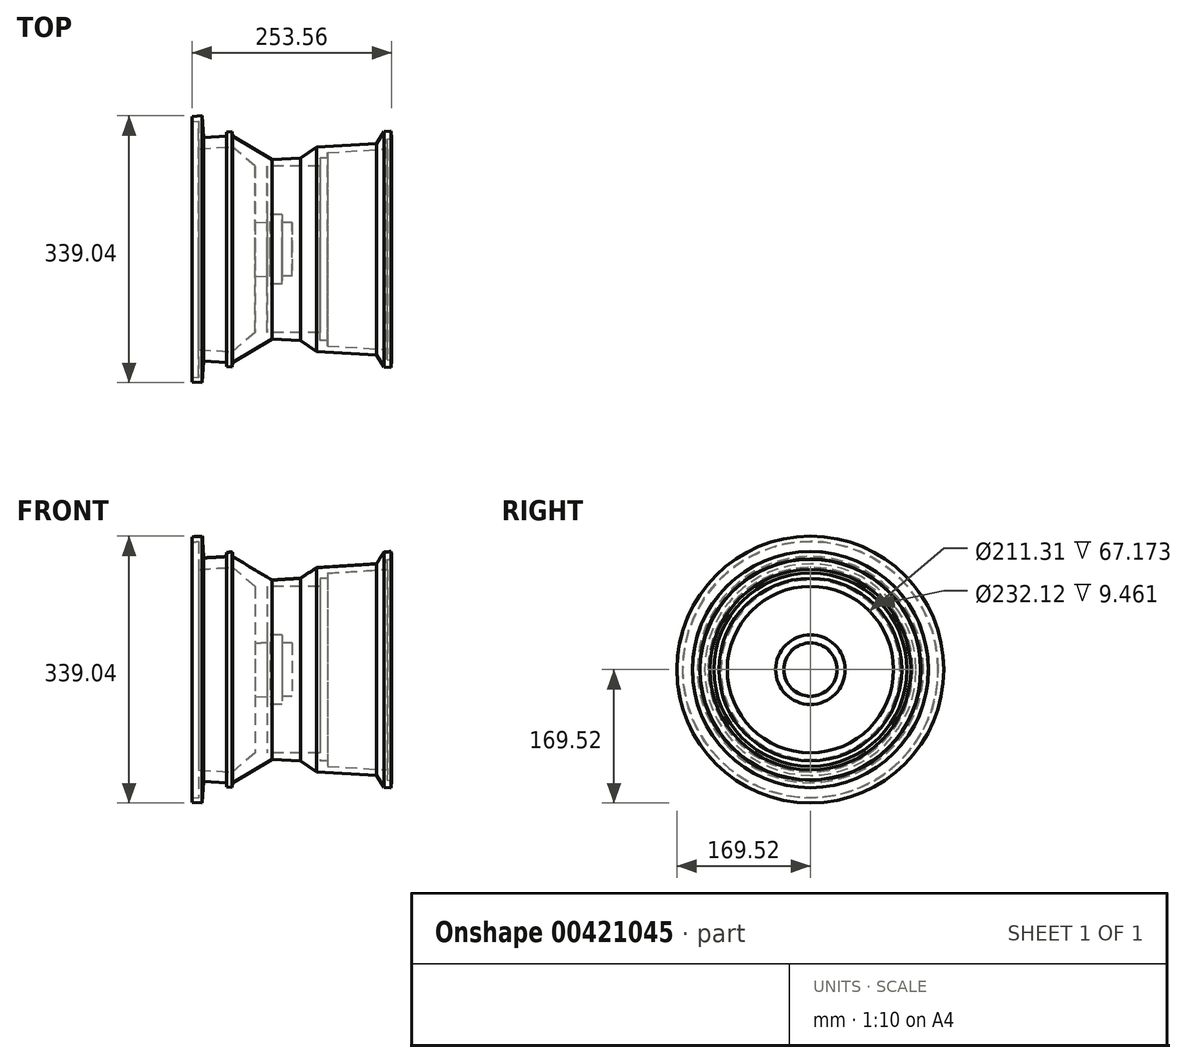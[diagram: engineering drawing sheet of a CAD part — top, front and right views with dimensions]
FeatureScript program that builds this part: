
annotation { "Feature Type Name" : "Feature", "Feature Type Description" : "" }
export const myFeature = defineFeature(function(context is Context, id is Id, definition is map)
    precondition{}
    {
        {
            var Q0;
            Q0=qCreatedBy(makeId("Front.planeOp"),FACE);
            var sketch = newSketch(context, id + "F0", { "sketchPlane" : qUnion([Q0])});
            skLineSegment(sketch, "E0", {"start": v(0, 0) * mm, "end": v(0, 33.75) * mm});
            skLineSegment(sketch, "E1", {"start": v(0, 33.75) * mm, "end": v(-12.72, 33.75) * mm});
            skLineSegment(sketch, "E2", {"start": v(-12.72, 33.75) * mm, "end": v(-12.72, 44.16) * mm});
            skLineSegment(sketch, "E3", {"start": v(-12.72, 44.16) * mm, "end": v(-31.64, 44.16) * mm});
            skLineSegment(sketch, "E4", {"start": v(-31.64, 44.16) * mm, "end": v(-31.64, 105.65) * mm});
            skLineSegment(sketch, "E5", {"start": v(-31.64, 105.65) * mm, "end": v(35.53, 105.65) * mm});
            skLineSegment(sketch, "E6", {"start": v(35.53, 105.65) * mm, "end": v(35.53, 116.06) * mm});
            skLineSegment(sketch, "E7", {"start": v(35.53, 116.06) * mm, "end": v(45, 116.06) * mm});
            skLineSegment(sketch, "E8", {"start": v(45, 116.06) * mm, "end": v(45, 122.68) * mm});
            skLineSegment(sketch, "E9", {"start": v(45, 122.68) * mm, "end": v(121.63, 127.41) * mm});
            skLineSegment(sketch, "E10", {"start": v(121.63, 127.41) * mm, "end": v(120.84, 140.06) * mm});
            skLineSegment(sketch, "E11", {"start": v(120.84, 140.06) * mm, "end": v(126.7, 140.42) * mm});
            skLineSegment(sketch, "E12", {"start": v(126.7, 140.42) * mm, "end": v(126.1, 150) * mm});
            skLineSegment(sketch, "E13", {"start": v(126.1, 150) * mm, "end": v(117.12, 149.44) * mm});
            skLineSegment(sketch, "E14", {"start": v(117.12, 149.44) * mm, "end": v(107.32, 134.35) * mm});
            skLineSegment(sketch, "E15", {"start": v(107.32, 134.35) * mm, "end": v(31.6, 129.67) * mm});
            skLineSegment(sketch, "E16", {"start": v(31.6, 129.67) * mm, "end": v(10.77, 116.06) * mm});
            skLineSegment(sketch, "E17", {"start": v(10.77, 116.06) * mm, "end": v(-25.33, 113.83) * mm});
            skLineSegment(sketch, "E18", {"start": v(-25.33, 113.83) * mm, "end": v(-75.4, 143.7) * mm});
            skLineSegment(sketch, "E19", {"start": v(-75.4, 143.7) * mm, "end": v(-75.76, 149.44) * mm});
            skLineSegment(sketch, "E20", {"start": v(-75.76, 149.44) * mm, "end": v(-83.2, 148.98) * mm});
            skLineSegment(sketch, "E21", {"start": v(-83.2, 148.98) * mm, "end": v(-82.87, 143.7) * mm});
            skLineSegment(sketch, "E22", {"start": v(-82.87, 143.7) * mm, "end": v(-112.12, 141.89) * mm});
            skLineSegment(sketch, "E23", {"start": v(-112.12, 141.89) * mm, "end": v(-113.82, 169.52) * mm});
            skLineSegment(sketch, "E24", {"start": v(-113.82, 169.52) * mm, "end": v(-126.86, 168.71) * mm});
            skLineSegment(sketch, "E25", {"start": v(-126.86, 168.71) * mm, "end": v(-126.46, 162.2) * mm});
            skLineSegment(sketch, "E26", {"start": v(-126.46, 162.2) * mm, "end": v(-118.38, 162.7) * mm});
            skLineSegment(sketch, "E27", {"start": v(-118.38, 162.7) * mm, "end": v(-118.38, 127.41) * mm});
            skLineSegment(sketch, "E28", {"start": v(-118.38, 127.41) * mm, "end": v(-75.4, 130.07) * mm});
            skLineSegment(sketch, "E29", {"start": v(-75.4, 130.07) * mm, "end": v(-46.85, 105.65) * mm});
            skLineSegment(sketch, "E30", {"start": v(-46.85, 105.65) * mm, "end": v(-46.85, 33.75) * mm});
            skLineSegment(sketch, "E31", {"start": v(-46.85, 33.75) * mm, "end": v(-27.79, 34.93) * mm});
            skLineSegment(sketch, "E32", {"start": v(-27.79, 34.93) * mm, "end": v(-27.79, 0) * mm});
            skLineSegment(sketch, "E33", {"start": v(-27.79, 0) * mm, "end": v(0, 0) * mm});
            skSolve(sketch);
        }
        {
            var Q0;
            Q0 = qSketchRegion(id + "F0", true);
            var Q1;
            Q1=sQuery(id+"F0.wireOp",EDGE,"E33");
            revolve(context, id + "F1", {"entities" : qUnion([Q0]), "axis" : qUnion([Q1]), "revolveType" : RevolveType.FULL});
        }
    });
